# Revit family: ARKOSLIGHT_Minimal Track Suspension 24V_Profile + Rubber Cable Xm
name_source: partatom
category: Lighting Fixtures
units: mm (PartAtom-declared; Revit-internal decimal feet)

## family parameters
Cut with Voids When Loaded = No
Host = Face
Light Source = No
Part Type = Normal
Room Calculation Point = No
Round Connector Dimension = Use Diameter
Shared = No

## types (4) — shared parameters
ARKOSLIGHT_Fixture Type = ACCESSORIES
ARKOSLIGHT_Model = ACCESSORIES
ARKOSLIGHT_Series = TRACK 24V ACCESSORIES
Apparent Load = 0 VA
Description = Select the number, feed type and length of profiles suitable for the defined length. End cap kit and other accessories not included
Manufacturer = ARKOSLIGHT
Model = ACCESSORIES
URL = https://www.arkoslight.com
zero-valued in all types: Default Elevation

## per-type parameters (varying)
| type | ARKOSLIGHT_Body Color | ARKOSLIGHT_Color | ARKOSLIGHT_Reference |
| A4000XY0WT - MINIMAL TRACK 24V SUSP PROFILE XM Y-FEED KIT WT + A3840001N - RUBBER CABLE | ARKOSLIGHT_Textured white | Textured white | A4000XY0WT |
| A4000XY0N - MINIMAL TRACK 24V SUSP PROFILE XM Y-FEED KIT N + A3840001N - RUBBER CABLE | ARKOSLIGHT_Black | Black | A4000XY0N |
| A3840X00N - MINIMAL TRACK 24V PROFILE XM N + U3840001N - RUBBER CABLE | ARKOSLIGHT_Black | Black | A3840X00N |
| A3840X00WT - MINIMAL TRACK 24V PROFILE XM WT + U3840001N - RUBBER CABLE | ARKOSLIGHT_Textured white | Textured white | A3840X00WT |

## geometry (parser evidence)
native form markers: Sweep x5
no freeform markers — native parametric forms only
